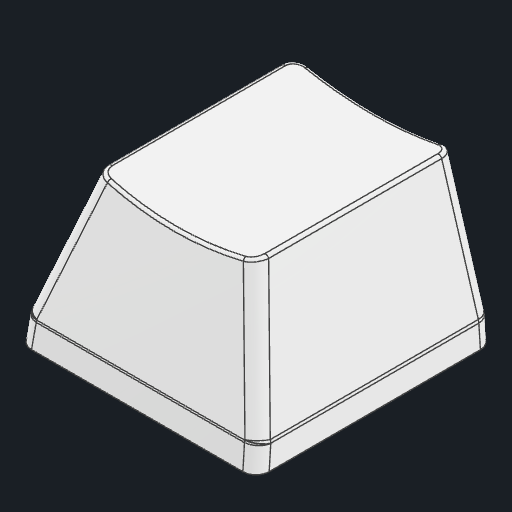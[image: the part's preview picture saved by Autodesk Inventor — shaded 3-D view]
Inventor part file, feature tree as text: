
AUTODESK INVENTOR PART (.ipt)
format: ipt  version: 2024.2 (Build 282272000, 272)  size: 982,528 bytes
history: native  units: mm
features: fillet x1
ambient origin geometry x8: Origin, YZ Plane, XZ Plane, XY Plane, X Axis, Y Axis, Z Axis, Center Point
bodies: Solid1 (feature_tree)
feature tree (1):
  fillet  "Fillet13"  [1 undecoded]
note: 1 required parameter value undecoded (feature->parameter linkage not recoverable at this tier; creation-order binding heuristic only, values carry confidence <= 0.55)
